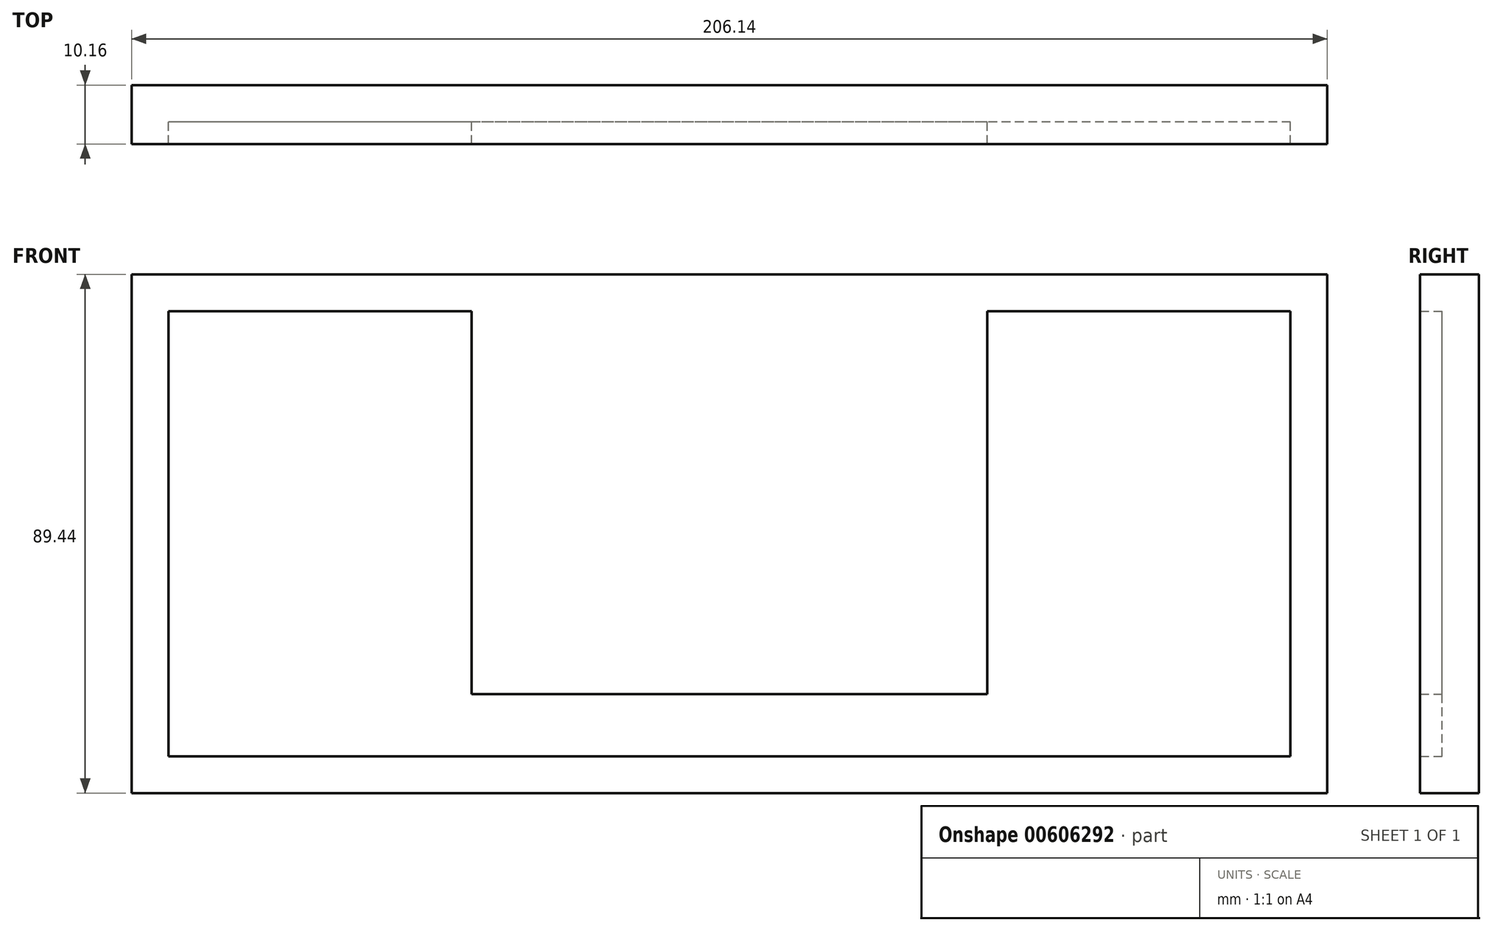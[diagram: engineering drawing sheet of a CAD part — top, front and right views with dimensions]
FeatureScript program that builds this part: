
annotation { "Feature Type Name" : "Feature", "Feature Type Description" : "" }
export const myFeature = defineFeature(function(context is Context, id is Id, definition is map)
    precondition{}
    {
        {
            var Q0;
            Q0=qCreatedBy(makeId("Front.planeOp"),FACE);
            var sketch = newSketch(context, id + "F0", { "sketchPlane" : qUnion([Q0])});
            skLineSegment(sketch, "E0.bottom", {"start": v(103.07, -44.72) * mm, "end": v(-103.07, -44.72) * mm});
            skLineSegment(sketch, "E0.top", {"start": v(103.07, 44.72) * mm, "end": v(-103.07, 44.72) * mm});
            skLineSegment(sketch, "E0.left", {"start": v(103.07, -44.72) * mm, "end": v(103.07, 44.72) * mm});
            skLineSegment(sketch, "E0.right", {"start": v(-103.07, -44.72) * mm, "end": v(-103.07, 44.72) * mm});
            skPoint(sketch, "E0.middle", {"position": v(0, 0) * mm});
            skSolve(sketch);
        }
        {
            var Q0;
            Q0 = qSketchRegion(id + "F0", true);
            extrude(context, id + "F1", {"entities" : qUnion([Q0]), "depth" : 10.16 * mm, "offsetDistance" : 25.4 * mm});
        }
        {
            var Q0;
            Q0=makeQuery(id+"F1.opExtrude","CAP_FACE",FACE,{"disambiguationData":[OSD([sQuery(id+"F0.wireOp",EDGE,"E0.bottom"),sQuery(id+"F0.wireOp",EDGE,"E0.top"),sQuery(id+"F0.wireOp",EDGE,"E0.left"),sQuery(id+"F0.wireOp",EDGE,"E0.right")])],"isStart":false});
            shell(context, id + "F2", {"entities" : qUnion([Q0]), "thickness" : 6.35 * mm});
        }
        {
            var Q0;
            Q0=makeQuery(id+"F2.opShell","OFFSET_FACE",FACE,{"disambiguationData":[OSD([sQuery(id+"F0.wireOp",EDGE,"E0.bottom"),sQuery(id+"F0.wireOp",EDGE,"E0.top"),sQuery(id+"F0.wireOp",EDGE,"E0.left"),sQuery(id+"F0.wireOp",EDGE,"E0.right")])]});
            var sketch = newSketch(context, id + "F3", { "sketchPlane" : qUnion([Q0])});
            skLineSegment(sketch, "E1.bottom", {"start": v(44.45, -27.67) * mm, "end": v(-44.45, -27.67) * mm});
            skLineSegment(sketch, "E1.top", {"start": v(44.45, 38.37) * mm, "end": v(-44.45, 38.37) * mm});
            skLineSegment(sketch, "E1.left", {"start": v(44.45, -27.67) * mm, "end": v(44.45, 38.37) * mm});
            skLineSegment(sketch, "E1.right", {"start": v(-44.45, -27.67) * mm, "end": v(-44.45, 38.37) * mm});
            skPoint(sketch, "E1.middle", {"position": v(0, 5.35) * mm});
            skSolve(sketch);
        }
        {
            var Q0;
            Q0 = qSketchRegion(id + "F3", true);
            var Q1;
            Q1=makeQuery(id+"F1.opExtrude","CAP_FACE",FACE,{"disambiguationData":[OSD([sQuery(id+"F0.wireOp",EDGE,"E0.bottom"),sQuery(id+"F0.wireOp",EDGE,"E0.top"),sQuery(id+"F0.wireOp",EDGE,"E0.left"),sQuery(id+"F0.wireOp",EDGE,"E0.right")])],"isStart":false});
            extrude(context, id + "F4", {"entities" : qUnion([Q0]), "operationType" : NewBodyOperationType.ADD, "endBound" : BoundingType.UP_TO_SURFACE, "depth" : 7.62 * mm, "endBoundEntityFace" : qUnion([Q1]), "offsetDistance" : 25.4 * mm});
        }
    });
